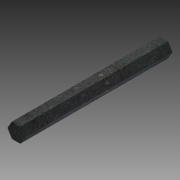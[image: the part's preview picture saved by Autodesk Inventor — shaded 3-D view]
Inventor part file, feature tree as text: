
AUTODESK INVENTOR PART (.ipt)
format: ipt  version: 2014 (Build 180170000, 170)  size: 81,920 bytes
history: native  units: in
note: dims shown in document units (in); Inventor stores cm internally (conversion verified against a paired STEP export)
features: extrude x1, sketch x1
ambient origin geometry x8: Origin, YZ Plane, XZ Plane, XY Plane, X Axis, Y Axis, Z Axis, Center Point
bodies: Solid1 (feature_tree)
feature tree (2):
  extrude  "Extrusion1"  Depth=5.0in TaperAngle=0.0deg
  sketch  "Sketch1"  dims[d0=0.5in d1=5.0in d2=0.0in]
